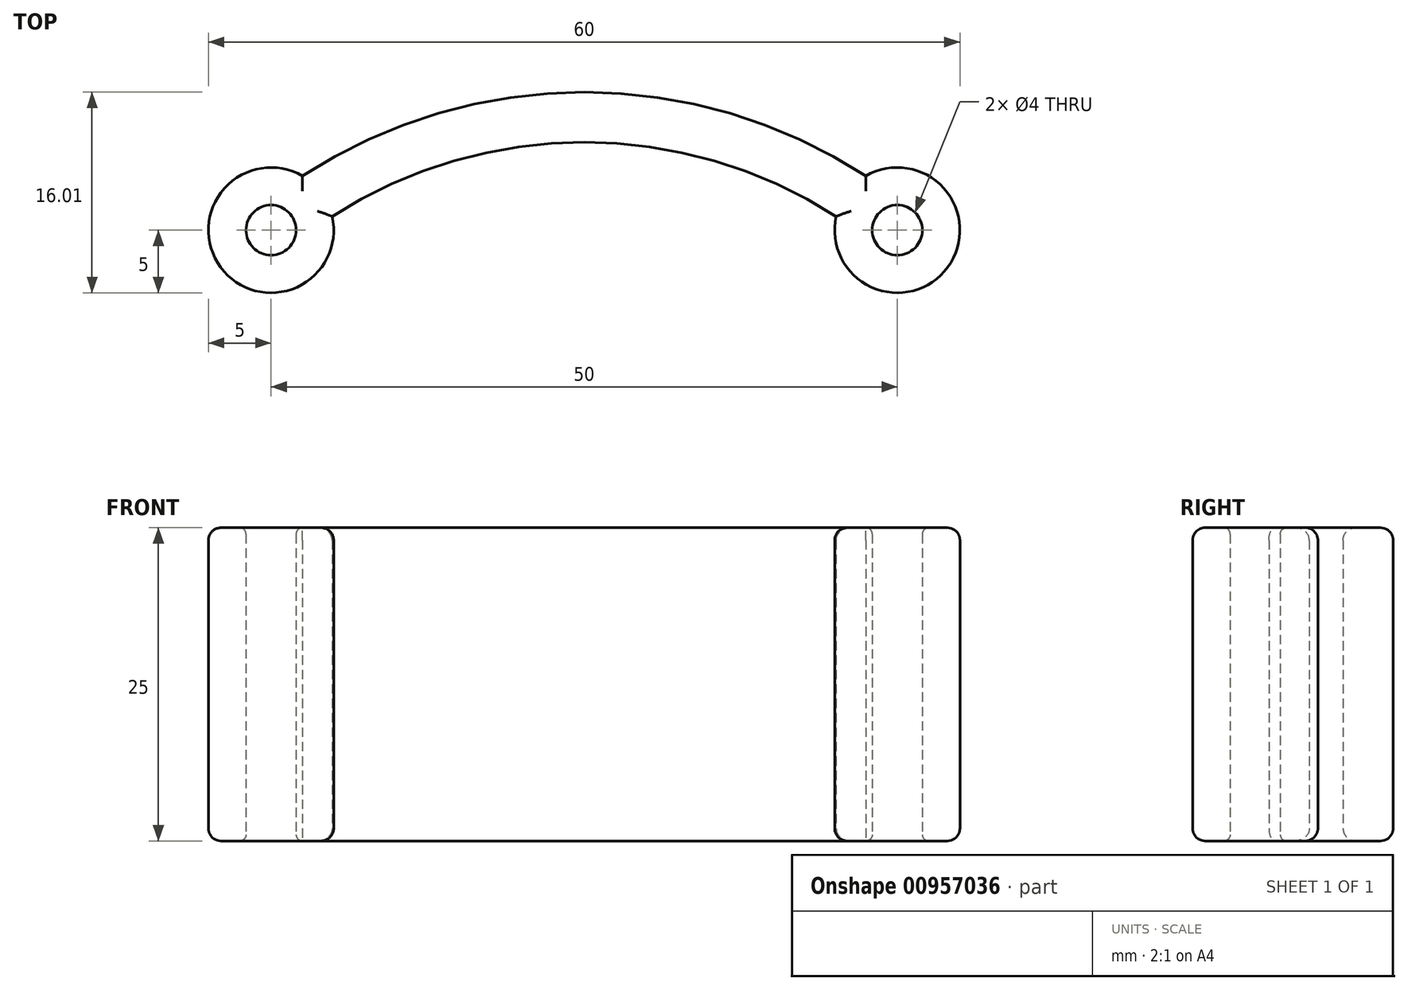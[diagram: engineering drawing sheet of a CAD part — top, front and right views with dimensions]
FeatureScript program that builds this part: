
annotation { "Feature Type Name" : "Feature", "Feature Type Description" : "" }
export const myFeature = defineFeature(function(context is Context, id is Id, definition is map)
    precondition{}
    {
        {
            var Q0;
            Q0=qCreatedBy(makeId("Top.planeOp"),FACE);
            var sketch = newSketch(context, id + "F0", { "sketchPlane" : qUnion([Q0])});
            skArc(sketch, "E0", {"start": v(2.5, 4.33) * mm, "mid": v(-4.03, -2.96) * mm, "end": v(4.88, 1.1) * mm});
            skCircle(sketch, "E1", {"center": v(0, 0) * mm, "radius": 2 * mm});
            skArc(sketch, "E2", {"start": v(45.12, 1.1) * mm, "mid": v(54.03, -2.96) * mm, "end": v(47.5, 4.33) * mm});
            skCircle(sketch, "E3", {"center": v(50, 0) * mm, "radius": 2 * mm});
            skArc(sketch, "E4.0", {"start": v(45.12, 1.1) * mm, "mid": v(25, 7) * mm, "end": v(4.88, 1.1) * mm});
            skArc(sketch, "E5.0", {"start": v(47.5, 4.33) * mm, "mid": v(25, 11) * mm, "end": v(2.5, 4.33) * mm});
            skSolve(sketch);
        }
        {
            var Q0;
            Q0 = qSketchRegion(id + "F0", true);
            extrude(context, id + "F1", {"entities" : qUnion([Q0]), "depth" : 25 * mm, "offsetDistance" : 25 * mm});
        }
        {
            var Q0;
            Q0=makeQuery(id+"F1.opExtrude","CAP_EDGE",EDGE,{"disambiguationData":[OSD([sQuery(id+"F0.wireOp",EDGE,"E1")])],"isStart":true});
            var Q1;
            Q1=makeQuery(id+"F1.opExtrude","CAP_EDGE",EDGE,{"disambiguationData":[OSD([sQuery(id+"F0.wireOp",EDGE,"E3")])],"isStart":true});
            var Q2;
            Q2=makeQuery(id+"F1.opExtrude","CAP_EDGE",EDGE,{"disambiguationData":[OSD([sQuery(id+"F0.wireOp",EDGE,"E3")])],"isStart":false});
            var Q3;
            Q3=makeQuery(id+"F1.opExtrude","CAP_EDGE",EDGE,{"disambiguationData":[OSD([sQuery(id+"F0.wireOp",EDGE,"E1")])],"isStart":false});
            fillet(context, id + "F2", {"entities" : qUnion([Q0, Q1, Q2, Q3]), "radius" : 0.5 * mm, "tangentPropagation" : true, "allowEdgeOverflow" : false});
        }
        {
            var Q0;
            Q0=makeQuery(id+"F1.opExtrude","CAP_EDGE",EDGE,{"disambiguationData":[OSD([sQuery(id+"F0.wireOp",EDGE,"E2")])],"isStart":false});
            var Q1;
            Q1=makeQuery(id+"F1.opExtrude","CAP_EDGE",EDGE,{"disambiguationData":[OSD([sQuery(id+"F0.wireOp",EDGE,"E4.0")])],"isStart":false});
            var Q2;
            Q2=makeQuery(id+"F1.opExtrude","CAP_EDGE",EDGE,{"disambiguationData":[OSD([sQuery(id+"F0.wireOp",EDGE,"E5.0")])],"isStart":false});
            var Q3;
            Q3=makeQuery(id+"F1.opExtrude","CAP_EDGE",EDGE,{"disambiguationData":[OSD([sQuery(id+"F0.wireOp",EDGE,"E0")])],"isStart":false});
            var Q4;
            Q4=makeQuery(id+"F1.opExtrude","CAP_EDGE",EDGE,{"disambiguationData":[OSD([sQuery(id+"F0.wireOp",EDGE,"E4.0")])],"isStart":true});
            var Q5;
            Q5=makeQuery(id+"F1.opExtrude","CAP_EDGE",EDGE,{"disambiguationData":[OSD([sQuery(id+"F0.wireOp",EDGE,"E0")])],"isStart":true});
            var Q6;
            Q6=makeQuery(id+"F1.opExtrude","CAP_EDGE",EDGE,{"disambiguationData":[OSD([sQuery(id+"F0.wireOp",EDGE,"E5.0")])],"isStart":true});
            var Q7;
            Q7=makeQuery(id+"F1.opExtrude","CAP_EDGE",EDGE,{"disambiguationData":[OSD([sQuery(id+"F0.wireOp",EDGE,"E2")])],"isStart":true});
            fillet(context, id + "F3", {"entities" : qUnion([Q0, Q1, Q2, Q3, Q4, Q5, Q6, Q7]), "radius" : 1 * mm, "tangentPropagation" : true, "allowEdgeOverflow" : false});
        }
    });
